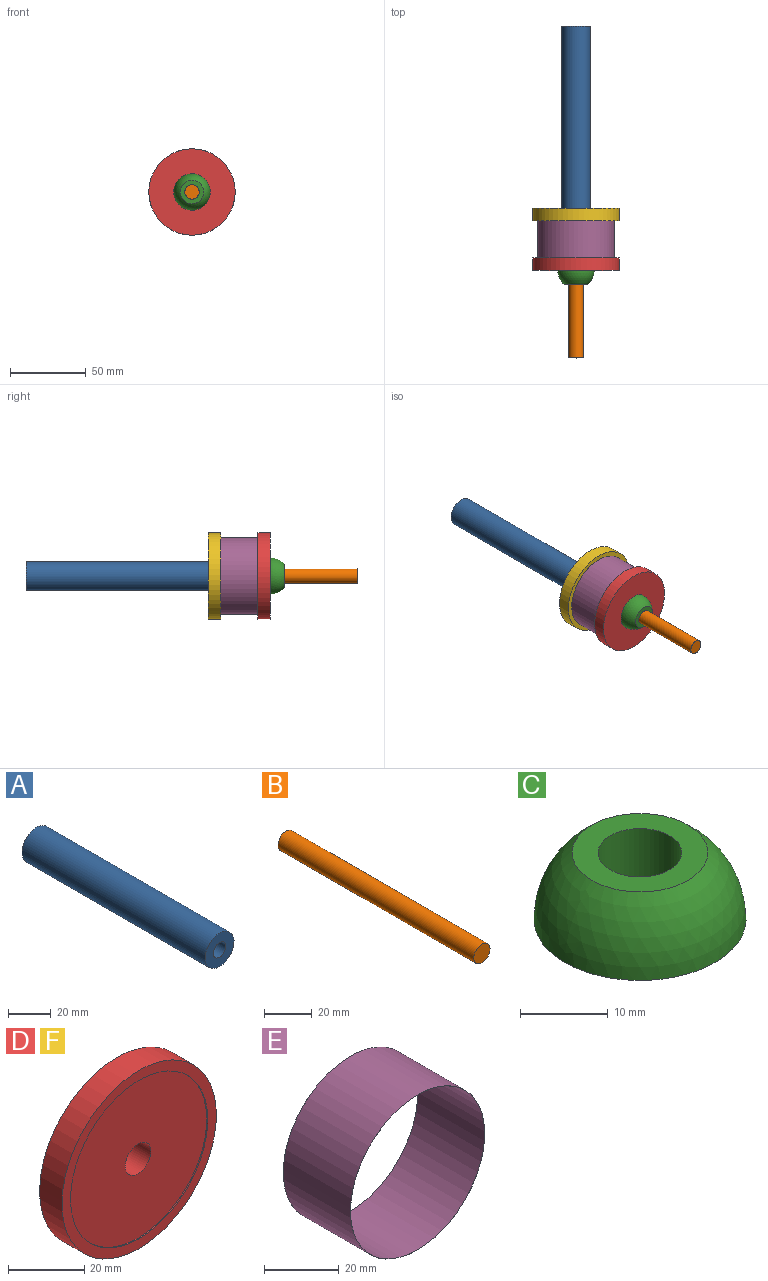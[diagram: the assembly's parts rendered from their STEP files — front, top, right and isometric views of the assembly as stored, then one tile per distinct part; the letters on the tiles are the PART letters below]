
ASSEMBLY  parts=6 mates=6
PART A: 7 faces, bbox 19.1x120.7x19.1 mm
  f0: cylinder r=9.53mm len=120.65mm, axis (0,1,0), area 7220.6mm2, adj f1,f2
  f1: plane 19.05x19.05mm, normal (0,-1,0), area 230.5mm2, adj f0,f3
  f2: plane 19.05x19.05mm, normal (0,1,0), area 207.7mm2, adj f0,f5
  f3: cylinder r=4.17mm len=38.1mm, axis (0,-1,0), area 997.6mm2, adj f1,f4
  f4: plane 8.33x8.33mm, normal (0,-1,0), area 54.6mm2, adj f3
  f5: cylinder r=4.96mm len=31.75mm, axis (0,1,0), area 989.7mm2, adj f2,f6
  f6: plane 9.92x9.92mm, normal (0,1,0), area 77.3mm2, adj f5
PART B: 3 faces, bbox 9.5x115.9x9.5 mm
  f0: cylinder r=4.76mm len=115.89mm, axis (0,1,0), area 3467.8mm2, adj f1,f2
  f1: plane 9.53x9.53mm, normal (0,-1,0), area 71.3mm2, adj f0
  f2: plane 9.53x9.53mm, normal (0,1,0), area 71.3mm2, adj f0
PART C: 4 faces, bbox 24.1x24.1x9.3 mm
  f0: plane 24.13x24.13mm, normal (0,0,-1), area 386mm2, adj f1,f3
  f1: sphere r=12.06mm, area 702.8mm2, adj f0,f2
  f2: plane 15.44x15.44mm, normal (0,0,1), area 116mm2, adj f1,f3
  f3: cylinder r=4.76mm len=9.53mm, axis (0,0,-1), area 277.4mm2, adj f0,f2
PART D: 6 faces, bbox 57.2x8.3x57.2 mm
  f0: cylinder r=4.76mm len=9.53mm, axis (0,1,0), area 235.6mm2, adj f3,f5
  f1: cylinder r=28.57mm len=57.15mm, axis (0,1,0), area 1482.1mm2, adj f2,f3
  f2: plane 57.15x57.15mm, normal (0,-1,0), area 538.4mm2, adj f1,f4
  f3: plane 57.15x57.15mm, normal (0,1,0), area 2494mm2, adj f0,f1
  f4: cylinder r=25.4mm len=50.8mm, axis (0,-1,0), area 60.8mm2, adj f2,f5
  f5: plane 50.8x50.8mm, normal (0,-1,0), area 1955.6mm2, adj f0,f4
PART E: 4 faces, bbox 50.8x25.4x50.8 mm
  f0: cylinder r=25.37mm len=50.75mm, axis (0,1,0), area 4049.6mm2, adj f2,f3
  f1: cylinder r=25.4mm len=50.8mm, axis (0,1,0), area 4053.7mm2, adj f2,f3
  f2: plane 50.8x50.8mm, normal (0,-1,0), area 4.1mm2, adj f0,f1
  f3: plane 50.8x50.8mm, normal (0,1,0), area 4.1mm2, adj f0,f1
PART F: same geometry as D
PLACE A t=(48.32,-12.61,-60.75)mm fixed
PLACE B t=(48.32,-114.07,-60.75)mm
PLACE C rot(axis=(1,0,0),90deg) t=(48.32,-114.08,-60.75)mm
PLACE D rot(axis=(1,0,0),180deg) t=(48.32,-114.08,-60.75)mm
PLACE E rot(axis=(1,0,0),0deg) t=(48.32,-80.81,-60.75)mm
PLACE F rot(axis=(1,0,0),0deg) t=(48.32,-72.93,-60.75)mm
MATE fastened E.f1 <-> D.f4  axis (0,-1,0) through (48.32,-106.21,-60.75)mm
MATE fastened A.f0 <-> F.f0  axis (0,-1,0) through (48.32,-72.93,-60.75)mm
MATE fastened E.f1 <-> F.f4  axis (0,1,0) through (48.32,-80.81,-60.75)mm
MATE fastened B.f0 <-> D.f1  axis (0,-1,0) through (48.32,-172.02,-60.75)mm
MATE fastened C.f3 <-> D.f0  axis (0,1,0) through (48.32,-114.08,-60.75)mm
MATE slider B.f0 <-> D.f0  axis (0,1,0) through (48.32,-114.07,-60.75)mm
